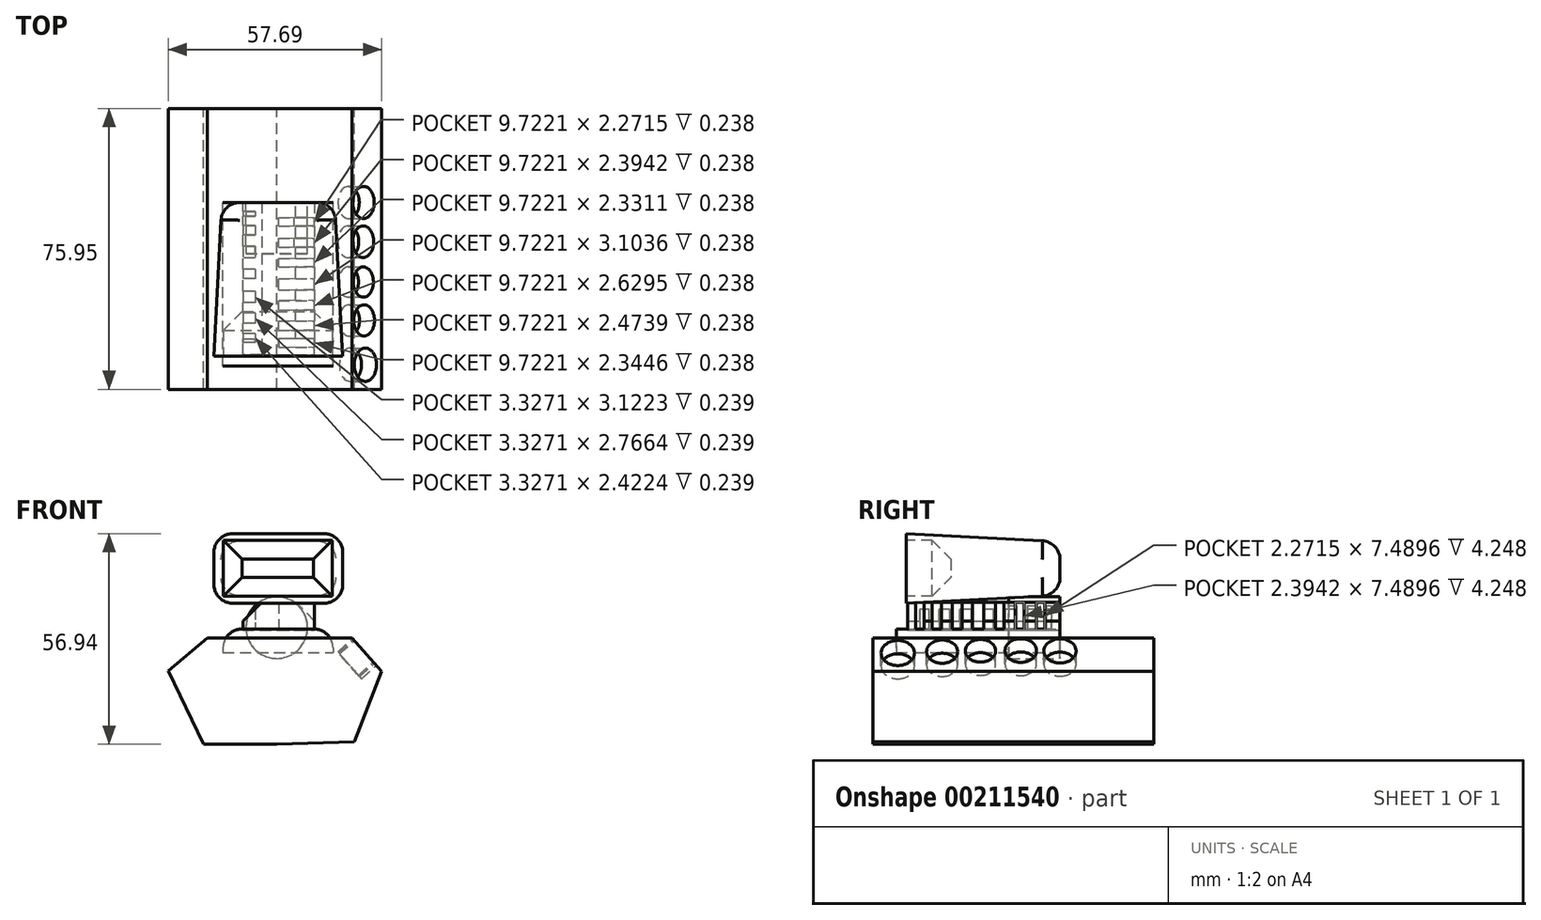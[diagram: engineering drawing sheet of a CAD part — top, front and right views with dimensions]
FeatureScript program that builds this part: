
annotation { "Feature Type Name" : "Feature", "Feature Type Description" : "" }
export const myFeature = defineFeature(function(context is Context, id is Id, definition is map)
    precondition{}
    {
        {
            var Q0;
            Q0=qCreatedBy(makeId("Front.planeOp"),FACE);
            var sketch = newSketch(context, id + "F0", { "sketchPlane" : qUnion([Q0])});
            skLineSegment(sketch, "E0.bottom", {"start": v(-14.82, 7.25) * mm, "end": v(15.66, 7.25) * mm});
            skLineSegment(sketch, "E0.top", {"start": v(-14.82, -7.2) * mm, "end": v(15.66, -7.2) * mm});
            skLineSegment(sketch, "E0.left", {"start": v(-14.82, 7.25) * mm, "end": v(-14.82, -7.2) * mm});
            skLineSegment(sketch, "E0.right", {"start": v(15.66, 7.25) * mm, "end": v(15.66, -7.2) * mm});
            skSolve(sketch);
        }
        {
            var Q0;
            Q0 = qSketchRegion(id + "F0", true);
            extrude(context, id + "F18", {"entities" : qUnion([Q0]), "depth" : 41.58 * mm, "hasDraft" : true, "draftAngle" : 3 * degree});
        }
        {
            var Q0;
            Q0=makeQuery(id+"F18.opExtrude","CAP_FACE",FACE,{"disambiguationData":[OSD([sQuery(id+"F0.wireOp",EDGE,"E0.bottom"),sQuery(id+"F0.wireOp",EDGE,"E0.top"),sQuery(id+"F0.wireOp",EDGE,"E0.left"),sQuery(id+"F0.wireOp",EDGE,"E0.right")])],"isStart":false});
            var sketch = newSketch(context, id + "F1", { "sketchPlane" : qUnion([Q0])});
            skLineSegment(sketch, "E1.bottom", {"start": v(-14.4, 7.64) * mm, "end": v(15.04, 7.64) * mm});
            skLineSegment(sketch, "E1.top", {"start": v(-14.4, -7.46) * mm, "end": v(15.04, -7.46) * mm});
            skLineSegment(sketch, "E1.left", {"start": v(-14.4, 7.64) * mm, "end": v(-14.4, -7.46) * mm});
            skLineSegment(sketch, "E1.right", {"start": v(15.04, 7.64) * mm, "end": v(15.04, -7.46) * mm});
            skSolve(sketch);
        }
        {
            var Q0;
            Q0 = qSketchRegion(id + "F1", true);
            extrude(context, id + "F2", {"entities" : qUnion([Q0]), "operationType" : NewBodyOperationType.REMOVE, "oppositeDirection" : true, "depth" : 12.12 * mm});
        }
        {
            var Q0;
            Q0=makeQuery(id+"F2.boolean.opBoolean","COPY",FACE,{"derivedFrom":makeQuery(id+"F2.opExtrude","CAP_FACE",FACE,{"disambiguationData":[OSD([sQuery(id+"F1.wireOp",EDGE,"E1.bottom"),sQuery(id+"F1.wireOp",EDGE,"E1.top"),sQuery(id+"F1.wireOp",EDGE,"E1.left"),sQuery(id+"F1.wireOp",EDGE,"E1.right")])],"isStart":false})});
            chamfer(context, id + "F19", {"entities" : qUnion([Q0]), "width" : 5.08 * mm, "tangentPropagation" : true});
        }
        {
            var Q0;
            Q0=makeQuery(id+"F18.opExtrude","CAP_FACE",FACE,{"disambiguationData":[OSD([sQuery(id+"F0.wireOp",EDGE,"E0.bottom"),sQuery(id+"F0.wireOp",EDGE,"E0.top"),sQuery(id+"F0.wireOp",EDGE,"E0.left"),sQuery(id+"F0.wireOp",EDGE,"E0.right")])],"isStart":true});
            fillet(context, id + "F3", {"entities" : qUnion([Q0]), "radius" : 5.08 * mm, "tangentPropagation" : true, "allowEdgeOverflow" : false});
        }
        {
            var Q0;
            Q0=makeQuery(id+"F18.opExtrude","SWEPT_EDGE",EDGE,{"disambiguationData":[OSD([sQuery(id+"F0.wireOp",EDGE,"E0.bottom"),sQuery(id+"F0.wireOp",EDGE,"E0.right")])]});
            var Q1;
            Q1=makeQuery(id+"F18.opExtrude","SWEPT_EDGE",EDGE,{"disambiguationData":[OSD([sQuery(id+"F0.wireOp",EDGE,"E0.top"),sQuery(id+"F0.wireOp",EDGE,"E0.right")])]});
            var Q2;
            Q2=makeQuery(id+"F18.opExtrude","SWEPT_EDGE",EDGE,{"disambiguationData":[OSD([sQuery(id+"F0.wireOp",EDGE,"E0.top"),sQuery(id+"F0.wireOp",EDGE,"E0.left")])]});
            var Q3;
            Q3=makeQuery(id+"F18.opExtrude","SWEPT_EDGE",EDGE,{"disambiguationData":[OSD([sQuery(id+"F0.wireOp",EDGE,"E0.bottom"),sQuery(id+"F0.wireOp",EDGE,"E0.left")])]});
            fillet(context, id + "F4", {"entities" : qUnion([Q0, Q1, Q2, Q3]), "radius" : 5.08 * mm, "tangentPropagation" : true, "allowEdgeOverflow" : false});
        }
        {
            var Q0;
            Q0=qCreatedBy(makeId("Front.planeOp"),FACE);
            var sketch = newSketch(context, id + "F20", { "sketchPlane" : qUnion([Q0])});
            skLineSegment(sketch, "E2", {"start": v(0, -18.81) * mm, "end": v(-18.8, -18.81) * mm});
            skLineSegment(sketch, "E3", {"start": v(-18.8, -18.81) * mm, "end": v(-29.35, -27.63) * mm});
            skLineSegment(sketch, "E4", {"start": v(-29.35, -27.63) * mm, "end": v(-19.82, -47.51) * mm});
            skLineSegment(sketch, "E5", {"start": v(-19.82, -47.51) * mm, "end": v(0, -47.51) * mm});
            skLineSegment(sketch, "E6", {"start": v(0, -18.81) * mm, "end": v(20.4, -18.81) * mm});
            skLineSegment(sketch, "E7", {"start": v(20.4, -18.81) * mm, "end": v(28.34, -27.79) * mm});
            skLineSegment(sketch, "E8", {"start": v(28.34, -27.79) * mm, "end": v(20.92, -46.83) * mm});
            skLineSegment(sketch, "E9", {"start": v(20.92, -46.83) * mm, "end": v(0, -47.51) * mm});
            skSolve(sketch);
        }
        {
            var Q0;
            Q0 = qSketchRegion(id + "F20", true);
            extrude(context, id + "F5", {"entities" : qUnion([Q0]), "depth" : 50.55 * mm});
        }
        {
            var Q0;
            Q0=makeQuery(id+"F5.opExtrude","CAP_FACE",FACE,{"disambiguationData":[OSD([sQuery(id+"F20.wireOp",EDGE,"E2"),sQuery(id+"F20.wireOp",EDGE,"E3"),sQuery(id+"F20.wireOp",EDGE,"E4"),sQuery(id+"F20.wireOp",EDGE,"E5"),sQuery(id+"F20.wireOp",EDGE,"E6"),sQuery(id+"F20.wireOp",EDGE,"E7"),sQuery(id+"F20.wireOp",EDGE,"E8"),sQuery(id+"F20.wireOp",EDGE,"E9")])],"isStart":true});
            extrude(context, id + "F6", {"entities" : qUnion([Q0]), "operationType" : NewBodyOperationType.ADD, "depth" : 25.4 * mm});
        }
        {
            var Q0;
            Q0=qCreatedBy(makeId("Front.planeOp"),FACE);
            var sketch = newSketch(context, id + "F7", { "sketchPlane" : qUnion([Q0])});
            skCircle(sketch, "E10", {"center": v(0, -15.97) * mm, "radius": 8.33 * mm});
            skSolve(sketch);
        }
        {
            var Q0;
            Q0 = qSketchRegion(id + "F7", true);
            extrude(context, id + "F8", {"entities" : qUnion([Q0]), "depth" : 13.9 * mm});
        }
        {
            var Q0;
            Q0=qCreatedBy(makeId("Front.planeOp"),FACE);
            var sketch = newSketch(context, id + "F9", { "sketchPlane" : qUnion([Q0])});
            skLineSegment(sketch, "E11.bottom", {"start": v(-14.53, -16.37) * mm, "end": v(15.2, -16.37) * mm});
            skLineSegment(sketch, "E11.top", {"start": v(-14.53, -22.75) * mm, "end": v(15.2, -22.75) * mm});
            skLineSegment(sketch, "E11.left", {"start": v(-14.53, -16.37) * mm, "end": v(-14.53, -22.75) * mm});
            skLineSegment(sketch, "E11.right", {"start": v(15.2, -16.37) * mm, "end": v(15.2, -22.75) * mm});
            skSolve(sketch);
        }
        {
            var Q0;
            Q0 = qSketchRegion(id + "F9", true);
            extrude(context, id + "F10", {"entities" : qUnion([Q0]), "depth" : 44.26 * mm});
        }
        {
            var Q0;
            Q0=makeQuery(id+"F10.opExtrude","SWEPT_EDGE",EDGE,{"disambiguationData":[OSD([sQuery(id+"F9.wireOp",EDGE,"E11.bottom"),sQuery(id+"F9.wireOp",EDGE,"E11.right")])]});
            var Q1;
            Q1=makeQuery(id+"F10.opExtrude","SWEPT_EDGE",EDGE,{"disambiguationData":[OSD([sQuery(id+"F9.wireOp",EDGE,"E11.bottom"),sQuery(id+"F9.wireOp",EDGE,"E11.left")])]});
            fillet(context, id + "F11", {"entities" : qUnion([Q0, Q1]), "radius" : 5.08 * mm, "tangentPropagation" : true, "allowEdgeOverflow" : false});
        }
        {
            var Q0;
            Q0=qCreatedBy(makeId("Front.planeOp"),FACE);
            var sketch = newSketch(context, id + "F12", { "sketchPlane" : qUnion([Q0])});
            skLineSegment(sketch, "E12.bottom", {"start": v(-9.16, -9.12) * mm, "end": v(10.22, -9.12) * mm});
            skLineSegment(sketch, "E12.top", {"start": v(-9.16, -16.61) * mm, "end": v(10.22, -16.61) * mm});
            skLineSegment(sketch, "E12.left", {"start": v(-9.16, -9.12) * mm, "end": v(-9.16, -16.61) * mm});
            skLineSegment(sketch, "E12.right", {"start": v(10.22, -9.12) * mm, "end": v(10.22, -16.61) * mm});
            skSolve(sketch);
        }
        {
            var Q0;
            Q0 = qSketchRegion(id + "F12", true);
            extrude(context, id + "F13", {"entities" : qUnion([Q0]), "depth" : 41.15 * mm});
        }
        {
            var Q0;
            Q0=makeQuery(id+"F13.opExtrude","SWEPT_FACE",FACE,{"disambiguationData":[OSD([sQuery(id+"F12.wireOp",EDGE,"E12.right")])]});
            var sketch = newSketch(context, id + "F21", { "sketchPlane" : qUnion([Q0])});
            skLineSegment(sketch, "E13.bottom", {"start": v(-39.1, -9.12) * mm, "end": v(-36.76, -9.12) * mm});
            skLineSegment(sketch, "E13.top", {"start": v(-39.1, -16.61) * mm, "end": v(-36.76, -16.61) * mm});
            skLineSegment(sketch, "E13.left", {"start": v(-39.1, -9.12) * mm, "end": v(-39.1, -16.61) * mm});
            skLineSegment(sketch, "E13.right", {"start": v(-36.76, -9.12) * mm, "end": v(-36.76, -16.61) * mm});
            skLineSegment(sketch, "E14.bottom", {"start": v(-34.53, -9.12) * mm, "end": v(-32.06, -9.12) * mm});
            skLineSegment(sketch, "E14.top", {"start": v(-34.53, -16.61) * mm, "end": v(-32.06, -16.61) * mm});
            skLineSegment(sketch, "E14.left", {"start": v(-34.53, -9.12) * mm, "end": v(-34.53, -16.61) * mm});
            skLineSegment(sketch, "E14.right", {"start": v(-32.06, -9.12) * mm, "end": v(-32.06, -16.61) * mm});
            skLineSegment(sketch, "E15.bottom", {"start": v(-29.14, -9.12) * mm, "end": v(-26.51, -9.12) * mm});
            skLineSegment(sketch, "E15.top", {"start": v(-29.14, -16.61) * mm, "end": v(-26.51, -16.61) * mm});
            skLineSegment(sketch, "E15.left", {"start": v(-29.14, -9.12) * mm, "end": v(-29.14, -16.61) * mm});
            skLineSegment(sketch, "E15.right", {"start": v(-26.51, -9.12) * mm, "end": v(-26.51, -16.61) * mm});
            skLineSegment(sketch, "E16.bottom", {"start": v(-23.68, -9.12) * mm, "end": v(-20.58, -9.12) * mm});
            skLineSegment(sketch, "E16.top", {"start": v(-23.68, -16.61) * mm, "end": v(-20.58, -16.61) * mm});
            skLineSegment(sketch, "E16.left", {"start": v(-23.68, -9.12) * mm, "end": v(-23.68, -16.61) * mm});
            skLineSegment(sketch, "E16.right", {"start": v(-20.58, -9.12) * mm, "end": v(-20.58, -16.61) * mm});
            skLineSegment(sketch, "E17.bottom", {"start": v(-17.46, -9.12) * mm, "end": v(-15.13, -9.12) * mm});
            skLineSegment(sketch, "E17.top", {"start": v(-17.46, -16.61) * mm, "end": v(-15.13, -16.61) * mm});
            skLineSegment(sketch, "E17.left", {"start": v(-17.46, -9.12) * mm, "end": v(-17.46, -16.61) * mm});
            skLineSegment(sketch, "E17.right", {"start": v(-15.13, -9.12) * mm, "end": v(-15.13, -16.61) * mm});
            skLineSegment(sketch, "E18.bottom", {"start": v(-12.13, -9.12) * mm, "end": v(-9.73, -9.12) * mm});
            skLineSegment(sketch, "E18.top", {"start": v(-12.13, -16.61) * mm, "end": v(-9.73, -16.61) * mm});
            skLineSegment(sketch, "E18.left", {"start": v(-12.13, -9.12) * mm, "end": v(-12.13, -16.61) * mm});
            skLineSegment(sketch, "E18.right", {"start": v(-9.73, -9.12) * mm, "end": v(-9.73, -16.61) * mm});
            skLineSegment(sketch, "E19.bottom", {"start": v(-6.34, -9.12) * mm, "end": v(-4.07, -9.12) * mm});
            skLineSegment(sketch, "E19.top", {"start": v(-6.34, -16.61) * mm, "end": v(-4.07, -16.61) * mm});
            skLineSegment(sketch, "E19.left", {"start": v(-6.34, -9.12) * mm, "end": v(-6.34, -16.61) * mm});
            skLineSegment(sketch, "E19.right", {"start": v(-4.07, -9.12) * mm, "end": v(-4.07, -16.61) * mm});
            skLineSegment(sketch, "E20.bottom", {"start": v(-4.07, -16.61) * mm, "end": v(-4.07, -16.61) * mm});
            skLineSegment(sketch, "E20.top", {"start": v(-4.07, -16.61) * mm, "end": v(-4.07, -16.61) * mm});
            skLineSegment(sketch, "E20.left", {"start": v(-4.07, -16.61) * mm, "end": v(-4.07, -16.61) * mm});
            skLineSegment(sketch, "E20.right", {"start": v(-4.07, -16.61) * mm, "end": v(-4.07, -16.61) * mm});
            skSolve(sketch);
        }
        {
            var Q0;
            Q0 = qSketchRegion(id + "F21", true);
            extrude(context, id + "F22", {"entities" : qUnion([Q0]), "operationType" : NewBodyOperationType.REMOVE, "oppositeDirection" : true, "depth" : 9.72 * mm});
        }
        {
            var Q0;
            Q0=makeQuery(id+"F13.opExtrude","SWEPT_FACE",FACE,{"disambiguationData":[OSD([sQuery(id+"F12.wireOp",EDGE,"E12.left")])]});
            var sketch = newSketch(context, id + "F14", { "sketchPlane" : qUnion([Q0])});
            skLineSegment(sketch, "E21.bottom", {"start": v(35.43, -9.12) * mm, "end": v(37.85, -9.12) * mm});
            skLineSegment(sketch, "E21.top", {"start": v(35.43, -16.61) * mm, "end": v(37.85, -16.61) * mm});
            skLineSegment(sketch, "E21.left", {"start": v(35.43, -9.12) * mm, "end": v(35.43, -16.61) * mm});
            skLineSegment(sketch, "E21.right", {"start": v(37.85, -9.12) * mm, "end": v(37.85, -16.61) * mm});
            skLineSegment(sketch, "E22.bottom", {"start": v(29.89, -9.12) * mm, "end": v(32.65, -9.12) * mm});
            skLineSegment(sketch, "E22.top", {"start": v(29.89, -16.61) * mm, "end": v(32.65, -16.61) * mm});
            skLineSegment(sketch, "E22.left", {"start": v(29.89, -9.12) * mm, "end": v(29.89, -16.61) * mm});
            skLineSegment(sketch, "E22.right", {"start": v(32.65, -9.12) * mm, "end": v(32.65, -16.61) * mm});
            skLineSegment(sketch, "E23.bottom", {"start": v(24.02, -9.12) * mm, "end": v(27.14, -9.12) * mm});
            skLineSegment(sketch, "E23.top", {"start": v(24.02, -16.61) * mm, "end": v(27.14, -16.61) * mm});
            skLineSegment(sketch, "E23.left", {"start": v(24.02, -9.12) * mm, "end": v(24.02, -16.61) * mm});
            skLineSegment(sketch, "E23.right", {"start": v(27.14, -9.12) * mm, "end": v(27.14, -16.61) * mm});
            skLineSegment(sketch, "E24.bottom", {"start": v(20.58, -9.12) * mm, "end": v(18.1, -9.12) * mm});
            skLineSegment(sketch, "E24.top", {"start": v(20.58, -16.61) * mm, "end": v(18.1, -16.61) * mm});
            skLineSegment(sketch, "E24.left", {"start": v(20.58, -9.12) * mm, "end": v(20.58, -16.61) * mm});
            skLineSegment(sketch, "E24.right", {"start": v(18.1, -9.12) * mm, "end": v(18.1, -16.61) * mm});
            skLineSegment(sketch, "E25.bottom", {"start": v(11.78, -9.12) * mm, "end": v(14.96, -9.12) * mm});
            skLineSegment(sketch, "E25.top", {"start": v(11.78, -16.61) * mm, "end": v(14.96, -16.61) * mm});
            skLineSegment(sketch, "E25.left", {"start": v(11.78, -9.12) * mm, "end": v(11.78, -16.61) * mm});
            skLineSegment(sketch, "E25.right", {"start": v(14.96, -9.12) * mm, "end": v(14.96, -16.61) * mm});
            skLineSegment(sketch, "E26.bottom", {"start": v(6.24, -9.12) * mm, "end": v(8.8, -9.12) * mm});
            skLineSegment(sketch, "E26.top", {"start": v(6.24, -16.61) * mm, "end": v(8.8, -16.61) * mm});
            skLineSegment(sketch, "E26.left", {"start": v(6.24, -9.12) * mm, "end": v(6.24, -16.61) * mm});
            skLineSegment(sketch, "E26.right", {"start": v(8.8, -9.12) * mm, "end": v(8.8, -16.61) * mm});
            skLineSegment(sketch, "E27.bottom", {"start": v(0, -9.12) * mm, "end": v(0, -9.12) * mm});
            skLineSegment(sketch, "E27.top", {"start": v(0, -9.12) * mm, "end": v(0, -9.12) * mm});
            skLineSegment(sketch, "E27.left", {"start": v(0, -9.12) * mm, "end": v(0, -9.12) * mm});
            skLineSegment(sketch, "E27.right", {"start": v(0, -9.12) * mm, "end": v(0, -9.12) * mm});
            skLineSegment(sketch, "E28.bottom", {"start": v(2.38, -9.12) * mm, "end": v(3.74, -9.12) * mm});
            skLineSegment(sketch, "E28.top", {"start": v(2.38, -16.61) * mm, "end": v(3.74, -16.61) * mm});
            skLineSegment(sketch, "E28.left", {"start": v(2.38, -9.12) * mm, "end": v(2.38, -16.61) * mm});
            skLineSegment(sketch, "E28.right", {"start": v(3.74, -9.12) * mm, "end": v(3.74, -16.61) * mm});
            skSolve(sketch);
        }
        {
            var Q0;
            Q0 = qSketchRegion(id + "F14", true);
            extrude(context, id + "F23", {"entities" : qUnion([Q0]), "operationType" : NewBodyOperationType.REMOVE, "oppositeDirection" : true, "depth" : 3.33 * mm});
        }
        {
            var Q0;
            {var subQ0=sQuery(id+"F12.wireOp",EDGE,"E12.bottom");var subQ1=sQuery(id+"F12.wireOp",EDGE,"E12.right");Q0=makeQuery(id+"F22.boolean.opBoolean","SPLIT",EDGE,{"disambiguationData":[TD([makeQuery(id+"F22.opExtrude","SWEPT_FACE",FACE,{"disambiguationData":[OSD([sQuery(id+"F21.wireOp",EDGE,"E13.right")])]})])],"derivedFrom":makeQuery(id+"F13.opExtrude","SWEPT_EDGE",EDGE,{"disambiguationData":[OSD([subQ0,subQ1])]})});}
            var Q1;
            {var subQ0=sQuery(id+"F12.wireOp",EDGE,"E12.bottom");var subQ1=sQuery(id+"F12.wireOp",EDGE,"E12.right");Q1=makeQuery(id+"F22.boolean.opBoolean","SPLIT",EDGE,{"disambiguationData":[TD([makeQuery(id+"F22.opExtrude","SWEPT_FACE",FACE,{"disambiguationData":[OSD([sQuery(id+"F21.wireOp",EDGE,"E14.right")])]})])],"derivedFrom":makeQuery(id+"F13.opExtrude","SWEPT_EDGE",EDGE,{"disambiguationData":[OSD([subQ0,subQ1])]})});}
            var Q2;
            {var subQ0=sQuery(id+"F12.wireOp",EDGE,"E12.bottom");var subQ1=sQuery(id+"F12.wireOp",EDGE,"E12.right");Q2=makeQuery(id+"F22.boolean.opBoolean","SPLIT",EDGE,{"disambiguationData":[TD([makeQuery(id+"F22.opExtrude","SWEPT_FACE",FACE,{"disambiguationData":[OSD([sQuery(id+"F21.wireOp",EDGE,"E15.right")])]})])],"derivedFrom":makeQuery(id+"F13.opExtrude","SWEPT_EDGE",EDGE,{"disambiguationData":[OSD([subQ0,subQ1])]})});}
            var Q3;
            {var subQ0=sQuery(id+"F12.wireOp",EDGE,"E12.bottom");var subQ1=sQuery(id+"F12.wireOp",EDGE,"E12.right");Q3=makeQuery(id+"F22.boolean.opBoolean","SPLIT",EDGE,{"disambiguationData":[TD([makeQuery(id+"F22.opExtrude","SWEPT_FACE",FACE,{"disambiguationData":[OSD([sQuery(id+"F21.wireOp",EDGE,"E16.right")])]})])],"derivedFrom":makeQuery(id+"F13.opExtrude","SWEPT_EDGE",EDGE,{"disambiguationData":[OSD([subQ0,subQ1])]})});}
            var Q4;
            {var subQ0=sQuery(id+"F12.wireOp",EDGE,"E12.bottom");var subQ1=sQuery(id+"F12.wireOp",EDGE,"E12.right");Q4=makeQuery(id+"F22.boolean.opBoolean","SPLIT",EDGE,{"disambiguationData":[TD([makeQuery(id+"F22.opExtrude","SWEPT_FACE",FACE,{"disambiguationData":[OSD([sQuery(id+"F21.wireOp",EDGE,"E17.right")])]})])],"derivedFrom":makeQuery(id+"F13.opExtrude","SWEPT_EDGE",EDGE,{"disambiguationData":[OSD([subQ0,subQ1])]})});}
            var Q5;
            {var subQ0=sQuery(id+"F12.wireOp",EDGE,"E12.bottom");var subQ1=sQuery(id+"F12.wireOp",EDGE,"E12.right");Q5=makeQuery(id+"F22.boolean.opBoolean","SPLIT",EDGE,{"disambiguationData":[TD([makeQuery(id+"F22.opExtrude","SWEPT_FACE",FACE,{"disambiguationData":[OSD([sQuery(id+"F21.wireOp",EDGE,"E18.right")])]})])],"derivedFrom":makeQuery(id+"F13.opExtrude","SWEPT_EDGE",EDGE,{"disambiguationData":[OSD([subQ0,subQ1])]})});}
            var Q6;
            {var subQ0=sQuery(id+"F12.wireOp",EDGE,"E12.bottom");var subQ1=sQuery(id+"F12.wireOp",EDGE,"E12.right");Q6=makeQuery(id+"F22.boolean.opBoolean","SPLIT",EDGE,{"disambiguationData":[TD([makeQuery(id+"F22.opExtrude","SWEPT_FACE",FACE,{"disambiguationData":[OSD([sQuery(id+"F21.wireOp",EDGE,"E19.right")])]})])],"derivedFrom":makeQuery(id+"F13.opExtrude","SWEPT_EDGE",EDGE,{"disambiguationData":[OSD([subQ0,subQ1])]})});}
            chamfer(context, id + "F24", {"entities" : qUnion([Q0, Q1, Q2, Q3, Q4, Q5, Q6]), "width" : 5.08 * mm, "tangentPropagation" : true});
        }
        {
            var Q0;
            {var subQ0=sQuery(id+"F12.wireOp",EDGE,"E12.bottom");var subQ1=sQuery(id+"F12.wireOp",EDGE,"E12.left");Q0=makeQuery(id+"F23.boolean.opBoolean","SPLIT",EDGE,{"disambiguationData":[TD([makeQuery(id+"F23.opExtrude","SWEPT_FACE",FACE,{"disambiguationData":[OSD([sQuery(id+"F14.wireOp",EDGE,"E28.left")])]})])],"derivedFrom":makeQuery(id+"F13.opExtrude","SWEPT_EDGE",EDGE,{"disambiguationData":[OSD([subQ0,subQ1])]})});}
            chamfer(context, id + "F15", {"entities" : qUnion([Q0]), "width" : 5.08 * mm, "tangentPropagation" : true});
        }
        {
            var Q0;
            {var subQ0=sQuery(id+"F20.wireOp",EDGE,"E7");Q0=makeQuery(id+"F6.boolean.opBoolean","MERGE",FACE,{"derivedFrom":[makeQuery(id+"F5.opExtrude","SWEPT_FACE",FACE,{"disambiguationData":[OSD([subQ0])]}),makeQuery(id+"F6.opExtrude","SWEPT_FACE",FACE,{"disambiguationData":[OSD([subQ0])]})]});}
            var sketch = newSketch(context, id + "F16", { "sketchPlane" : qUnion([Q0])});
            skCircle(sketch, "E29", {"center": v(-43.86, -32.97) * mm, "radius": 4.52 * mm});
            skCircle(sketch, "E30", {"center": v(-31.88, -32.48) * mm, "radius": 4.2 * mm});
            skCircle(sketch, "E31", {"center": v(-21.5, -32.16) * mm, "radius": 4.1 * mm});
            skCircle(sketch, "E32", {"center": v(-10.6, -32.08) * mm, "radius": 4.28 * mm});
            skCircle(sketch, "E33", {"center": v(0, -32.23) * mm, "radius": 4.36 * mm});
            skSolve(sketch);
        }
        {
            var Q0;
            Q0 = qSketchRegion(id + "F16", true);
            extrude(context, id + "F25", {"entities" : qUnion([Q0]), "operationType" : NewBodyOperationType.REMOVE, "oppositeDirection" : true, "depth" : 5.4 * mm});
        }
    });
